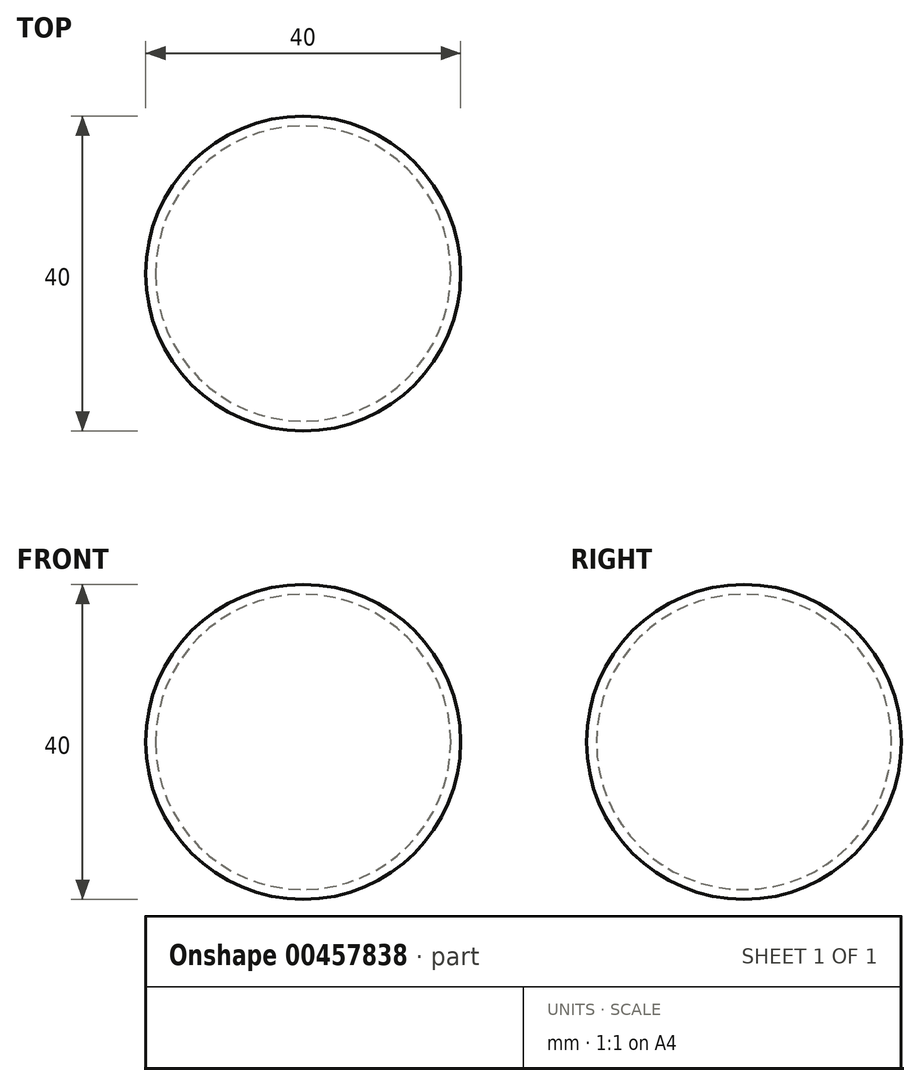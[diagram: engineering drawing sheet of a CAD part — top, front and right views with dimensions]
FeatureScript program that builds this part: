
annotation { "Feature Type Name" : "Feature", "Feature Type Description" : "" }
export const myFeature = defineFeature(function(context is Context, id is Id, definition is map)
    precondition{}
    {
        {
            var Q0;
            Q0=qCreatedBy(makeId("Top.planeOp"),FACE);
            var sketch = newSketch(context, id + "F0", { "sketchPlane" : qUnion([Q0])});
            skArc(sketch, "E0", {"start": v(20, 0) * mm, "mid": v(0, 20) * mm, "end": v(-20, 0) * mm});
            skLineSegment(sketch, "E1", {"start": v(-20, 0) * mm, "end": v(20, 0) * mm});
            skArc(sketch, "E2", {"start": v(18.75, 0) * mm, "mid": v(0, 18.75) * mm, "end": v(-18.75, 0) * mm});
            skSolve(sketch);
        }
        {
            var Q0;
            {var subQ0=sQuery(id+"F0.wireOp",EDGE,"E0");Q0=makeQuery(id+"F0.imprint","IMPRINT",FACE,{"disambiguationData":[TD([[makeQuery(id+"F0.imprint","IMPRINT",EDGE,{"derivedFrom":subQ0}),1.0]])]});}
            var Q1;
            Q1=sQuery(id+"F0.wireOp",EDGE,"E1");
            revolve(context, id + "F1", {"entities" : qUnion([Q0]), "axis" : qUnion([Q1]), "revolveType" : RevolveType.FULL});
        }
    });
